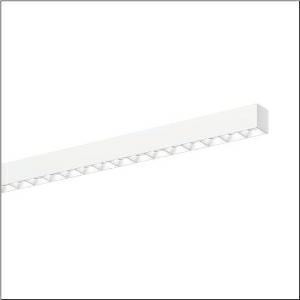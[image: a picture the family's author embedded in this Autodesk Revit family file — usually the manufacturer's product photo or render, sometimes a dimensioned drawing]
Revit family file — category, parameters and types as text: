
# Revit family: silica_21_51mx26db45wb
name_source: partatom
category: Lighting Fixtures
units: mm (PartAtom-declared; Revit-internal decimal feet)

## family parameters
Cut with Voids When Loaded = No
Host = Face
Light Source = No
Part Type = Normal
Room Calculation Point = No
Round Connector Dimension = Use Diameter
Shared = No

## types (1)
- --- (1 x LED, 5400 lm, 29.3 W, 4000K)
    Apparent Load = 29 VA
    CIE Flux Codes = 83 98 100 100 100
    Color Rendering = 80
    Color Temperature = 4000K
    Default Elevation = 1800 mm
    Description = Silica 21, office luminaire, primary light control with darklight reflector, of PMMA, white, CAT 2 (L<= 3000cd/m²), light emission: direct distribution, primary light characteristic: symmetric, installation type: surface-mounted, LED, rated luminous flux: 5.400lm, luminous efficacy: 184lm/W, light colour: 840, colour temperature: 4000K, control gear: DALI 2, with terminal, 3+2-pole, max. 2.5mm², mains connection: 220..240V, AC, 50/60Hz, rated input power: 29.3W, luminaire housing, of aluminium, traffic white (RAL 9016), length: 1.504mm, width: 53mm, height: 53mm, protection rating (complete): IP20, insulation class (complete): insulation class I (protective earthing), certification: CE, permissible operating ambient temperature: 0..+35°C, standard: EN 50419, packaging unit: 1 piece
    Height = 53 mm
    Lamp = 1 x LED
    Lamp Light Flux = 5400 lm
    Lamp Power = 29.3 W
    Lamp count = 1
    Length = 1504 mm
    Luminous efficacy = 184 lm/W
    Manufacturer = Siteco
    ModVariant = No
    Model = 51MX26DB45WB
    Mounting Place = Ceiling
    Mounting Type = Surface mounted
    Number of Poles = 1
    OnlyDefault = Yes
    Power Factor = 1
    Product Name = Silica 21
    Product group = office luminaire | ceiling mounted
    ProductGroupID = 301
    Protection Class = Protection class I
    Protection Degree = IP 20
    RLX_Detail_Level = 1
    RLX_Emergency_Light_Flux = 0 lm
    RLX_Emergency_Type = 0
    RLX_Emergency_Type_DB = No
    RlxData = <blob elided: 41801 chars, md5=b64b9d10>
    Socket = socket
    Standby Power = 0 W
    System Light Flux = 5400 lm
    System Power = 29 W
    Type Comments = factory setting: luminous flux: 100 % | dim-lin: 254 | 336 mA
    Type Image = l_1335934.jpg
    URL = http://relux.com
    VarID = @adj_124461
    Voltage = 0 V
    Weight = 0.00 kg
    Width = 53 mm

## geometry (parser evidence)
native form markers: Blend x4, Sweep x12
no freeform markers — native parametric forms only
